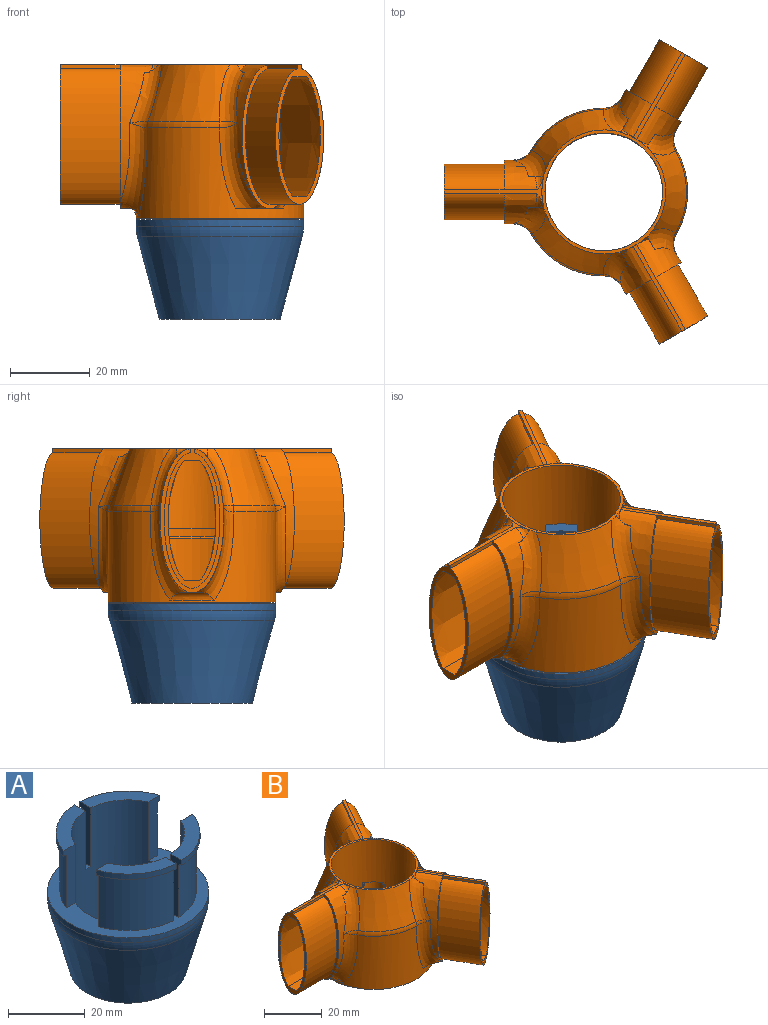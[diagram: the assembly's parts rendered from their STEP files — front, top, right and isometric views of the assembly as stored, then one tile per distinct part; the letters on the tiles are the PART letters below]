
ASSEMBLY  parts=2 mates=1
PART A: 34 faces, bbox 45.5x45.5x43.9 mm
  f0: cylinder r=14.75mm len=42.94mm, axis (0,0,1), area 3442.1mm2, adj f1,f2,f3,f14,f16,f20,f21,f22
  f1: plane 16.76x12.72mm, normal (0,0,1), area 76.7mm2, adj f0,f4,f21,f27
  f2: plane 16.76x12.72mm, normal (0,0,1), area 76.7mm2, adj f0,f5,f26,f28
  f3: plane 16.76x12.72mm, normal (0,0,1), area 76.7mm2, adj f0,f6,f24,f25
  f4: cylinder r=18.75mm len=16.76mm, axis (0,0,-1), area 38mm2, adj f1,f10,f21,f27
  f5: cylinder r=18.75mm len=16.76mm, axis (0,0,-1), area 38mm2, adj f2,f11,f26,f28
  f6: cylinder r=18.75mm len=16.76mm, axis (0,0,-1), area 38mm2, adj f3,f12,f24,f25
  f7: cylinder r=17.75mm len=16.5mm, axis (0,0,-1), area 342.5mm2, adj f20,f21,f27,f31
  f8: cylinder r=17.75mm len=16.5mm, axis (0,0,-1), area 342.5mm2, adj f20,f26,f28,f30
  f9: cylinder r=17.75mm len=16.5mm, axis (0,0,-1), area 342.5mm2, adj f20,f24,f25,f33
  f10: plane 16.76x12.72mm, normal (0,0,-1), area 11mm2, adj f4,f21,f27,f31
  f11: plane 16.76x12.72mm, normal (0,0,-1), area 11mm2, adj f5,f26,f28,f30
  f12: plane 16.76x12.72mm, normal (0,0,-1), area 11mm2, adj f6,f24,f25,f33
  f13: cylinder r=21mm len=42mm, axis (0,0,1), area 222.1mm2, adj f20,f29
  f14: plane 16.76x12.72mm, normal (0,0,1), area 76.7mm2, adj f0,f17,f22,f23
  f15: cone r=21mm half-angle=15deg, axis (0,0,1), area 2411.1mm2, adj f16,f29
  f16: torus R=15.75mm, axis (0,0,-1), area 81.3mm2, adj f0,f15
  f17: cylinder r=18.75mm len=16.76mm, axis (0,0,-1), area 38mm2, adj f14,f19,f22,f23
  f18: cylinder r=17.75mm len=16.5mm, axis (0,0,-1), area 342.5mm2, adj f20,f22,f23,f32
  f19: plane 16.76x12.72mm, normal (0,0,-1), area 11mm2, adj f17,f22,f23,f32
  f20: plane 42x42mm, normal (0,0,1), area 481.4mm2, adj f0,f7,f8,f9,f13,f18,f21,f22
  f21: plane 18.7x4.29mm, normal (0,1,0), area 62.3mm2, adj f0,f1,f4,f7,f10,f20,f31
  f22: plane 18.7x4.29mm, normal (0,-1,0), area 62.3mm2, adj f0,f14,f17,f18,f19,f20,f32
  f23: plane 18.71x4.02mm, normal (1,0,0), area 58mm2, adj f0,f14,f17,f18,f19,f20,f32
  f24: plane 18.71x4.02mm, normal (-1,0,0), area 58mm2, adj f0,f3,f6,f9,f12,f20,f33
  f25: plane 18.7x4.29mm, normal (0,-1,0), area 62.3mm2, adj f0,f3,f6,f9,f12,f20,f33
  f26: plane 18.7x4.29mm, normal (0,1,0), area 62.3mm2, adj f0,f2,f5,f8,f11,f20,f30
  f27: plane 18.71x4.02mm, normal (1,0,0), area 58mm2, adj f0,f1,f4,f7,f10,f20,f31
  f28: plane 18.71x4.02mm, normal (-1,0,0), area 58mm2, adj f0,f2,f5,f8,f11,f20,f30
  f29: torus R=11mm, axis (0,0,-1), area 343.6mm2, adj f13,f15
  f30: torus R=18.25mm, axis (0,0,1), area 16.5mm2, adj f8,f11,f26,f28
  f31: torus R=18.25mm, axis (0,0,1), area 16.5mm2, adj f7,f10,f21,f27
  f32: torus R=18.25mm, axis (0,0,1), area 16.5mm2, adj f18,f19,f22,f23
  f33: torus R=18.25mm, axis (0,0,1), area 16.5mm2, adj f9,f12,f24,f25
PART B: 131 faces, bbox 67.5x77.7x44.4 mm
  f0: cylinder r=19mm len=5.23mm, axis (0,0,1), area 11.6mm2, adj f8,f16,f34,f109
  f1: cylinder r=19mm len=22.06mm, axis (0,0,1), area 47.1mm2, adj f14,f19,f116,f120
  f2: cylinder r=19mm len=22.06mm, axis (0,0,1), area 47.1mm2, adj f7,f15,f112,f116
  f3: cylinder r=19mm len=22.06mm, axis (0,0,1), area 47.1mm2, adj f5,f106,f109,f112
  f4: cylinder r=14.75mm len=29.5mm, axis (0,0,-1), area 1614.3mm2, adj f13,f14,f15,f16,f30,f34,f35,f43
  f5: plane 22.06x3.67mm, normal (0,0,1), area 11.4mm2, adj f3,f109,f112,f124
  f6: plane 5.23x2.76mm, normal (0,0,1), area 2.7mm2, adj f17,f30,f120,f127
  f7: plane 22.06x3.67mm, normal (0,0,1), area 11.4mm2, adj f2,f112,f116,f125
  f8: plane 5.23x2.76mm, normal (0,0,1), area 2.7mm2, adj f0,f34,f109,f123
  f9: cylinder r=18mm len=16mm, axis (0,0,1), area 94.8mm2, adj f21,f22,f34,f109,f123
  f10: cylinder r=18mm len=19.56mm, axis (0,0,1), area 330.9mm2, adj f22,f116,f120,f126
  f11: cylinder r=18mm len=19.56mm, axis (0,0,1), area 330.9mm2, adj f22,f112,f116,f125
  f12: cylinder r=18mm len=19.56mm, axis (0,0,1), area 330.9mm2, adj f22,f109,f112,f124
  f13: plane 5.18x5.08mm, normal (0,0,-1), area 13.9mm2, adj f4,f17,f30,f120,f121
  f14: plane 22.06x6.13mm, normal (0,0,-1), area 79.5mm2, adj f1,f4,f116,f117,f120,f122
  f15: plane 22.06x6.13mm, normal (0,0,-1), area 79.5mm2, adj f2,f4,f112,f113,f115,f116
  f16: plane 5.18x5.08mm, normal (0,0,-1), area 13.9mm2, adj f0,f4,f34,f107,f109
  f17: cylinder r=19mm len=5.23mm, axis (0,0,1), area 11.6mm2, adj f6,f13,f30,f120
  f18: plane 8.34x7.61mm, normal (1,0,0), area 46.3mm2, adj f20,f21,f22,f30,f34,f38
  f19: plane 22.06x3.67mm, normal (0,0,1), area 11.4mm2, adj f1,f116,f120,f126
  f20: plane 8.71x0.94mm, normal (0.17,0.99,0), area 8.1mm2, adj f18,f22,f30,f105
  f21: plane 8.71x0.94mm, normal (0.17,-0.99,0), area 8.1mm2, adj f9,f18,f22,f34
  f22: plane 42x42mm, normal (0,0,-1), area 312.1mm2, adj f9,f10,f11,f12,f18,f20,f21,f45
  f23: cone r=15.54mm half-angle=20deg, axis (0,0,-1), area 303.7mm2, adj f27,f43,f50,f94
  f24: cone r=15.54mm half-angle=20deg, axis (0,0,-1), area 303.7mm2, adj f29,f43,f48,f59
  f25: cone r=15.54mm half-angle=20deg, axis (0,0,-1), area 303.7mm2, adj f28,f43,f61,f93
  f26: cone r=15.54mm half-angle=20deg, axis (0,0,-1), area 7.5mm2, adj f43,f84,f85,f86,f91,f92
  f27: torus R=16mm, axis (0,0,1), area 38.3mm2, adj f23,f45,f55,f87
  f28: torus R=16mm, axis (0,0,1), area 38.3mm2, adj f25,f45,f57,f60,f61,f82
  f29: torus R=16mm, axis (0,0,1), area 38.3mm2, adj f24,f45,f53,f56,f58,f59
  f30: extruded ~30x26.53mm, area 774.8mm2, adj f4,f6,f13,f17,f18,f20,f35,f38
  f31: extruded ~34.25x8.06mm, area 123.5mm2, adj f37,f42,f47,f48,f49,f129
  f32: plane 15x1.01mm, normal (0,-1,0), area 15.2mm2, adj f36,f37,f39,f42
  f33: plane 15x1.01mm, normal (0,1,0), area 15.2mm2, adj f36,f37,f39,f42
  f34: extruded ~30x26.53mm, area 774.8mm2, adj f0,f4,f8,f9,f16,f18,f21,f35
  f35: plane 25.38x3.94mm, normal (0,0,-1), area 99.7mm2, adj f4,f30,f34,f39
  f36: extruded ~33.96x15mm, area 1165.7mm2, adj f32,f33,f39,f42
  f37: plane 25.04x7.09mm, normal (0,0,1), area 26.8mm2, adj f31,f32,f33,f39,f40,f77,f128,f129
  f38: plane 21.5x3.94mm, normal (0,0,1), area 84.7mm2, adj f18,f30,f34,f39
  f39: plane 34.97x14mm, normal (-1,0,0), area 81.8mm2, adj f30,f32,f33,f34,f35,f36,f37,f38
  f40: extruded ~34.25x8.06mm, area 123.5mm2, adj f37,f42,f46,f50,f51,f128
  f41: plane 5.38x2.26mm, normal (0,0,-1), area 7mm2, adj f42,f49,f51,f130
  f42: plane 36.29x16.35mm, normal (-1,0,0), area 81mm2, adj f31,f32,f33,f36,f40,f41,f49,f51
  f43: plane 31.17x31.17mm, normal (0,0,1), area 76.3mm2, adj f4,f23,f24,f25,f26,f44,f46,f47
  f44: cone r=15.54mm half-angle=20deg, axis (0,0,-1), area 7.5mm2, adj f43,f62,f63,f66,f69,f75
  f45: cylinder r=21mm len=42mm, axis (0,0,-1), area 1762.5mm2, adj f22,f27,f28,f29,f49,f51,f53,f55
  f46: plane 4.24x2.4mm, normal (0,-1,0), area 1.8mm2, adj f40,f43,f50,f77,f128
  f47: plane 4.25x2.4mm, normal (0,1,0), area 1.8mm2, adj f31,f43,f48,f77,f129
  f48: bspline ~19.74x9.06mm, area 75.6mm2, adj f24,f31,f43,f47,f52,f53
  f49: bspline ~29.39x10.05mm, area 131.5mm2, adj f31,f41,f42,f45,f52,f130
  f50: bspline ~19.28x8.73mm, area 75.6mm2, adj f23,f40,f43,f46,f54,f55
  f51: bspline ~29.38x9.97mm, area 131.5mm2, adj f40,f41,f42,f45,f54,f130
  f52: bspline ~5.13x3.62mm, area 3.6mm2, adj f48,f49,f53
  f53: bspline ~1.71x0.29mm, area 0mm2, adj f29,f45,f48,f52
  f54: bspline ~4.67x2.61mm, area 3.6mm2, adj f50,f51,f55
  f55: bspline ~1.71x0.28mm, area 0mm2, adj f27,f45,f50,f54
  f56: bspline ~4.47x2.81mm, area 5.6mm2, adj f29,f58,f59
  f57: bspline ~6.18x1.79mm, area 4.8mm2, adj f28,f60,f61
  f58: bspline ~29.38x12.19mm, area 124.6mm2, adj f29,f45,f56,f64,f65,f66
  f59: bspline ~19.28x9.83mm, area 75.6mm2, adj f24,f29,f43,f56,f63,f66
  f60: bspline ~29.39x11.58mm, area 124.6mm2, adj f28,f45,f57,f64,f65,f75
  f61: bspline ~19.74x9.03mm, area 75.6mm2, adj f25,f28,f43,f57,f62,f75
  f62: plane 3.37x2.04mm, normal (-0.87,-0.5,0), area 2.2mm2, adj f43,f44,f61,f75
  f63: plane 3.37x2.04mm, normal (0.87,0.5,0), area 2.2mm2, adj f43,f44,f59,f66
  f64: plane 35.94x13.86mm, normal (0.5,-0.87,0), area 81mm2, adj f58,f60,f65,f66,f70,f73,f74,f75
  f65: plane 11.96x8.41mm, normal (0,0,-1), area 23.2mm2, adj f45,f58,f60,f64
  f66: extruded ~34.25x11.94mm, area 117.9mm2, adj f44,f58,f59,f63,f64,f69
  f67: plane 34.97x12.12mm, normal (0.5,-0.87,0), area 81.8mm2, adj f68,f69,f70,f71,f72,f73,f74,f76
  f68: plane 18.51x12.96mm, normal (0,0,1), area 75mm2, adj f67,f72,f76,f101
  f69: plane 21.68x13.09mm, normal (0,0,1), area 24.5mm2, adj f44,f66,f67,f73,f74,f75
  f70: extruded ~33.96x19.99mm, area 1165.7mm2, adj f64,f67,f73,f74
  f71: plane 22.31x15.16mm, normal (0,0,-1), area 92.2mm2, adj f67,f72,f76,f103
  f72: extruded ~30x22.35mm, area 642.9mm2, adj f67,f68,f71,f101,f103
  f73: plane 12.99x7.5mm, normal (-0.87,-0.5,0), area 15.2mm2, adj f64,f67,f69,f70
  f74: plane 12.99x7.5mm, normal (0.87,0.5,0), area 15.2mm2, adj f64,f67,f69,f70
  f75: extruded ~34.25x11.94mm, area 117.9mm2, adj f44,f60,f61,f62,f64,f69
  f76: extruded ~30x22.35mm, area 642.9mm2, adj f67,f68,f71,f101,f103
  f77: cone r=15.54mm half-angle=20deg, axis (0,0,-1), area 0.4mm2, adj f37,f43,f46,f47,f128,f129
  f78: extruded ~33.96x19.99mm, area 1165.7mm2, adj f79,f80,f81,f95
  f79: plane 12.99x7.5mm, normal (-0.87,0.5,0), area 15.2mm2, adj f78,f81,f85,f95
  f80: plane 12.99x7.5mm, normal (0.87,-0.5,0), area 15.2mm2, adj f78,f81,f85,f95
  f81: plane 36.29x14.21mm, normal (0.5,0.87,0), area 81mm2, adj f78,f79,f80,f83,f84,f86,f89,f90
  f82: bspline ~6.18x1.79mm, area 5.6mm2, adj f28,f90,f93
  f83: plane 13.41x9.86mm, normal (0,0,-1), area 23.2mm2, adj f45,f81,f89,f90
  f84: extruded ~34.25x11.94mm, area 117.9mm2, adj f26,f81,f85,f89,f91,f94
  f85: plane 21.68x13.09mm, normal (0,0,1), area 24.5mm2, adj f26,f79,f80,f84,f86,f95
  f86: extruded ~34.25x11.94mm, area 117.9mm2, adj f26,f81,f85,f90,f92,f93
  f87: bspline ~1.71x0.3mm, area 0mm2, adj f27,f45,f88,f94,f104
  f88: bspline ~5.57x2.81mm, area 4.9mm2, adj f87,f89,f94,f104
  f89: bspline ~29.39x12.3mm, area 129.5mm2, adj f45,f81,f83,f84,f88
  f90: bspline ~29.38x11.51mm, area 129.5mm2, adj f45,f81,f82,f83,f86
  f91: plane 3.37x2.04mm, normal (0.87,-0.5,0), area 2.2mm2, adj f26,f43,f84,f94
  f92: plane 3.89x2.56mm, normal (-0.87,0.5,0), area 2.2mm2, adj f26,f43,f86,f93
  f93: bspline ~19.28x9.16mm, area 77.2mm2, adj f25,f43,f82,f86,f92
  f94: bspline ~19.74x9.87mm, area 75.6mm2, adj f23,f43,f84,f87,f88,f91
  f95: plane 34.97x12.12mm, normal (0.5,0.87,0), area 81.8mm2, adj f78,f79,f80,f85,f96,f97,f98,f99
  f96: extruded ~30x22.35mm, area 642.9mm2, adj f95,f98,f99,f100,f102
  f97: extruded ~30x22.35mm, area 642.9mm2, adj f95,f98,f99,f100,f102
  f98: plane 18.51x12.96mm, normal (0,0,1), area 75mm2, adj f95,f96,f97,f100
  f99: plane 22.31x15.16mm, normal (0,0,-1), area 92.2mm2, adj f95,f96,f97,f102
  f100: cylinder r=21mm len=18mm, axis (0,0,-1), area 184.4mm2, adj f96,f97,f98,f102
  f101: cylinder r=21mm len=18mm, axis (0,0,-1), area 184.4mm2, adj f68,f72,f76,f103
  f102: cone r=15.54mm half-angle=20deg, axis (0,0,-1), area 119.2mm2, adj f96,f97,f99,f100
  f103: cone r=15.54mm half-angle=20deg, axis (0,0,-1), area 119.2mm2, adj f71,f72,f76,f101
  f104: torus R=16mm, axis (0,0,1), area 0mm2, adj f87,f88
  f105: cylinder r=18mm len=16mm, axis (0,0,1), area 94.8mm2, adj f20,f22,f30,f120,f127
  f106: plane 22.06x6.13mm, normal (0,0,-1), area 79.5mm2, adj f3,f4,f108,f109,f111,f112
  f107: plane 2x1.46mm, normal (0.71,0.71,0), area 4.1mm2, adj f4,f16,f109,f110
  f108: plane 2x1.46mm, normal (-0.71,-0.71,0), area 4.1mm2, adj f4,f106,f109,f110
  f109: cylinder r=4mm len=20.5mm, axis (0,0,1), area 201.6mm2, adj f0,f3,f5,f8,f9,f12,f16,f22
  f110: plane 8.29x8.29mm, normal (0,0,-1), area 38.7mm2, adj f4,f107,f108,f109
  f111: plane 2x1.46mm, normal (0.71,-0.71,0), area 4.1mm2, adj f4,f106,f112,f114
  f112: cylinder r=4mm len=20.5mm, axis (0,0,1), area 201.6mm2, adj f2,f3,f5,f7,f11,f12,f15,f22
  f113: plane 2x1.46mm, normal (-0.71,0.71,0), area 4.1mm2, adj f4,f15,f112,f114
  f114: plane 8.29x8.29mm, normal (0,0,-1), area 38.7mm2, adj f4,f111,f112,f113
  f115: plane 2x1.46mm, normal (-0.71,-0.71,0), area 4.1mm2, adj f4,f15,f116,f118
  f116: cylinder r=4mm len=20.5mm, axis (0,0,1), area 201.6mm2, adj f1,f2,f7,f10,f11,f14,f15,f19
  f117: plane 2x1.46mm, normal (0.71,0.71,0), area 4.1mm2, adj f4,f14,f116,f118
  f118: plane 8.29x8.29mm, normal (0,0,-1), area 38.7mm2, adj f4,f115,f116,f117
  f119: plane 8.29x8.29mm, normal (0,0,-1), area 38.7mm2, adj f4,f120,f121,f122
  f120: cylinder r=4mm len=20.5mm, axis (0,0,1), area 201.6mm2, adj f1,f6,f10,f13,f14,f17,f19,f22
  f121: plane 2x1.46mm, normal (0.71,-0.71,0), area 4.1mm2, adj f4,f13,f119,f120
  f122: plane 2x1.46mm, normal (-0.71,0.71,0), area 4.1mm2, adj f4,f14,f119,f120
  f123: torus R=18.5mm, axis (0,0,1), area 3.7mm2, adj f8,f9,f34,f109
  f124: torus R=18.5mm, axis (0,0,1), area 16.7mm2, adj f5,f12,f109,f112
  f125: torus R=18.5mm, axis (0,0,1), area 16.7mm2, adj f7,f11,f112,f116
  f126: torus R=18.5mm, axis (0,0,1), area 16.7mm2, adj f10,f19,f116,f120
  f127: torus R=18.5mm, axis (0,0,1), area 3.7mm2, adj f6,f30,f105,f120
  f128: bspline ~5.02x4mm, area 5.4mm2, adj f37,f40,f46,f77
  f129: bspline ~5.13x4.14mm, area 5.4mm2, adj f31,f37,f47,f77
  f130: torus R=23mm, axis (0,0,-1), area 26mm2, adj f41,f45,f49,f51
PLACE A t=(8.44,-0.22,-27.15)mm
PLACE B t=(8.44,-0.22,-6.28)mm
MATE fastened A.f0 <-> B.f23  axis (0,0,1) through (8.44,-0.22,-8.45)mm
